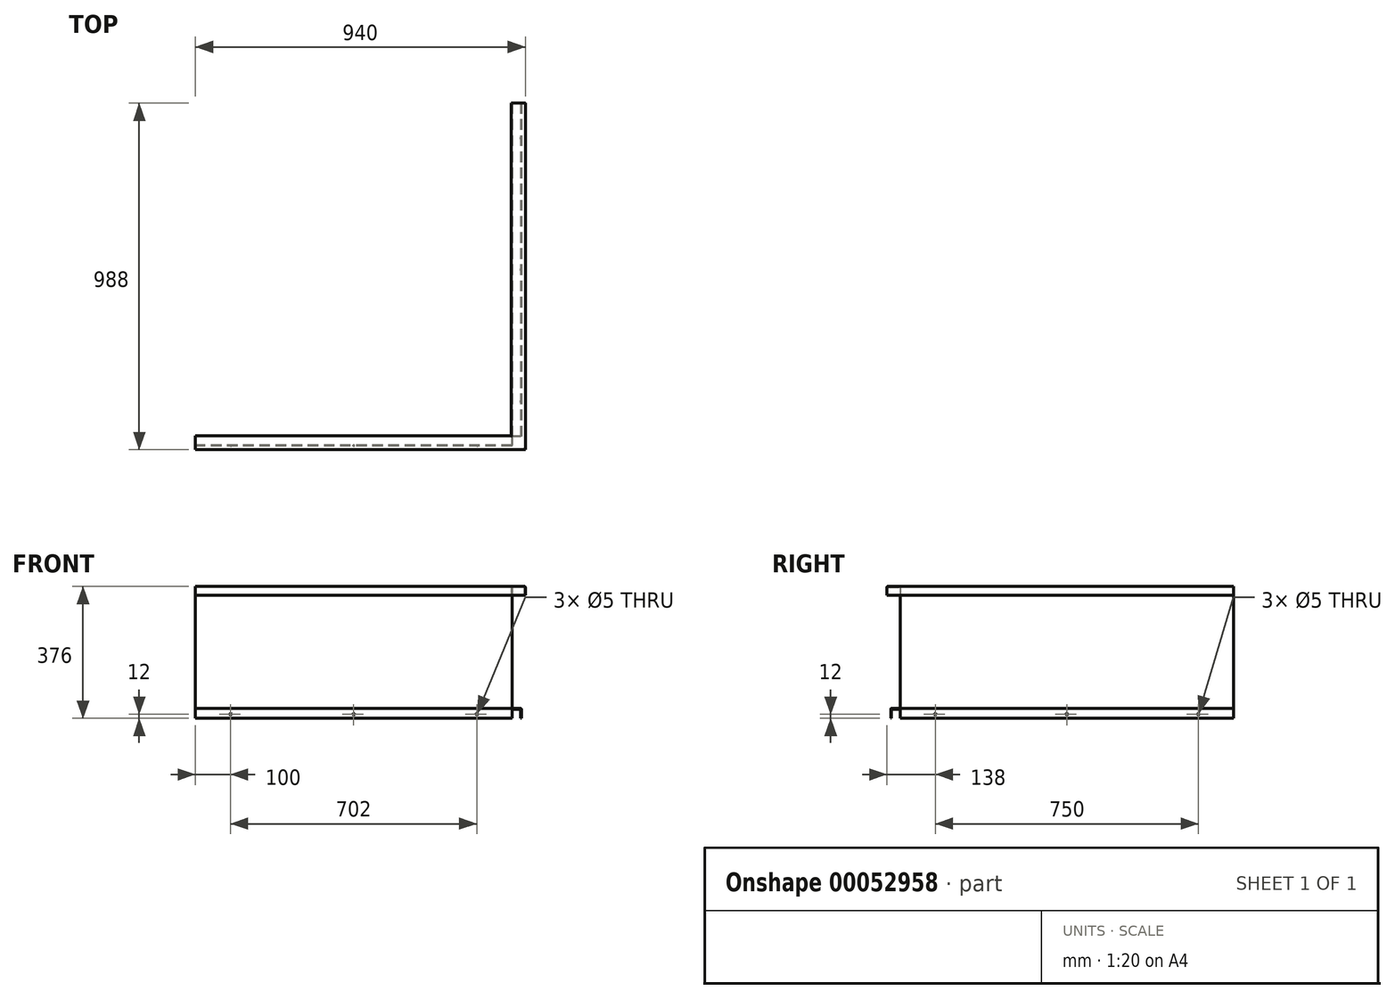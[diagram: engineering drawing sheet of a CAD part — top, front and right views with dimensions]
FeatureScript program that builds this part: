
annotation { "Feature Type Name" : "Feature", "Feature Type Description" : "" }
export const myFeature = defineFeature(function(context is Context, id is Id, definition is map)
    precondition{}
    {
        {
            var Q0;
            Q0=qCreatedBy(makeId("Front.planeOp"),FACE);
            var sketch = newSketch(context, id + "F0", { "sketchPlane" : qUnion([Q0])});
            skLineSegment(sketch, "E0", {"start": v(38, -25) * mm, "end": v(38, -2) * mm});
            skLineSegment(sketch, "E1", {"start": v(38, -2) * mm, "end": v(2, -2) * mm});
            skLineSegment(sketch, "E2", {"start": v(2, -2) * mm, "end": v(2, -348) * mm});
            skLineSegment(sketch, "E3", {"start": v(2, -348) * mm, "end": v(29, -348) * mm});
            skLineSegment(sketch, "E4", {"start": v(29, -348) * mm, "end": v(29, -376) * mm});
            skLineSegment(sketch, "E5.0", {"start": v(27, -350) * mm, "end": v(27, -376) * mm});
            skLineSegment(sketch, "E5.1", {"start": v(40, -25) * mm, "end": v(40, 0) * mm});
            skLineSegment(sketch, "E5.2", {"start": v(40, 0) * mm, "end": v(0, 0) * mm});
            skLineSegment(sketch, "E5.3", {"start": v(0, 0) * mm, "end": v(0, -350) * mm});
            skLineSegment(sketch, "E5.4", {"start": v(0, -350) * mm, "end": v(27, -350) * mm});
            skLineSegment(sketch, "E6", {"start": v(27, -376) * mm, "end": v(29, -376) * mm});
            skLineSegment(sketch, "E7", {"start": v(38, -25) * mm, "end": v(40, -25) * mm});
            skSolve(sketch);
        }
        {
            var Q0;
            Q0=qCreatedBy(makeId("Top.planeOp"),FACE);
            var sketch = newSketch(context, id + "F1", { "sketchPlane" : qUnion([Q0])});
            skLineSegment(sketch, "E8", {"start": v(0, 0) * mm, "end": v(0, -948) * mm});
            skLineSegment(sketch, "E9", {"start": v(0, -948) * mm, "end": v(-900, -948) * mm});
            skSolve(sketch);
        }
        {
            var Q0;
            Q0 = qSketchRegion(id + "F0", true);
            var Q1;
            Q1 = qConstructionFilter(qBodyType(qCreatedBy(id + "F1" ,EDGE), BodyType.WIRE), ConstructionObject.NO);
            sweep(context, id + "F2", {"profiles" : qUnion([Q0]), "path" : qUnion([Q1])});
        }
        {
            var Q0;
            Q0=makeQuery(id+"F2.opSweep","SWEPT_FACE",FACE,{"disambiguationData":[OSD([sQuery(id+"F0.wireOp",EDGE,"E3"),sQuery(id+"F1.wireOp",EDGE,"E8")])]});
            var sketch = newSketch(context, id + "F3", { "sketchPlane" : qUnion([Q0])});
            skLineSegment(sketch, "E10.bottom", {"start": v(2, -950) * mm, "end": v(29, -950) * mm});
            skLineSegment(sketch, "E10.top", {"start": v(2, -977) * mm, "end": v(29, -977) * mm});
            skLineSegment(sketch, "E10.left", {"start": v(2, -950) * mm, "end": v(2, -977) * mm});
            skLineSegment(sketch, "E10.right", {"start": v(29, -950) * mm, "end": v(29, -977) * mm});
            skSolve(sketch);
        }
        {
            var Q0;
            Q0 = qSketchRegion(id + "F3", true);
            extrude(context, id + "F4", {"entities" : qUnion([Q0]), "operationType" : NewBodyOperationType.REMOVE, "oppositeDirection" : true, "depth" : 30 * mm});
        }
        {
            var Q0;
            Q0=makeQuery(id+"F2.opSweep","SWEPT_EDGE",EDGE,{"disambiguationData":[OSD([sQuery(id+"F0.wireOp",EDGE,"E3"),sQuery(id+"F0.wireOp",EDGE,"E4"),sQuery(id+"F1.wireOp",EDGE,"E8")])]});
            var Q1;
            Q1=makeQuery(id+"F2.opSweep","SWEPT_EDGE",EDGE,{"disambiguationData":[OSD([sQuery(id+"F0.wireOp",EDGE,"E2"),sQuery(id+"F0.wireOp",EDGE,"E3"),sQuery(id+"F1.wireOp",EDGE,"E8")])]});
            var Q2;
            Q2=makeQuery(id+"F2.opSweep","SWEPT_EDGE",EDGE,{"disambiguationData":[OSD([sQuery(id+"F0.wireOp",EDGE,"E5.1"),sQuery(id+"F0.wireOp",EDGE,"E5.2"),sQuery(id+"F1.wireOp",EDGE,"E8")])]});
            var Q3;
            Q3=makeQuery(id+"F2.opSweep","SWEPT_EDGE",EDGE,{"disambiguationData":[OSD([sQuery(id+"F0.wireOp",EDGE,"E5.2"),sQuery(id+"F0.wireOp",EDGE,"E5.3"),sQuery(id+"F1.wireOp",EDGE,"E8")])]});
            var Q4;
            Q4=makeQuery(id+"F2.opSweep","SWEPT_EDGE",EDGE,{"disambiguationData":[OSD([sQuery(id+"F0.wireOp",EDGE,"E5.0"),sQuery(id+"F0.wireOp",EDGE,"E5.4"),sQuery(id+"F1.wireOp",EDGE,"E8")])]});
            var Q5;
            Q5=makeQuery(id+"F2.opSweep","SWEPT_EDGE",EDGE,{"disambiguationData":[OSD([sQuery(id+"F0.wireOp",EDGE,"E5.3"),sQuery(id+"F0.wireOp",EDGE,"E5.4"),sQuery(id+"F1.wireOp",EDGE,"E8")])]});
            var Q6;
            Q6=makeQuery(id+"F2.opSweep","SWEPT_EDGE",EDGE,{"disambiguationData":[OSD([sQuery(id+"F0.wireOp",EDGE,"E0"),sQuery(id+"F0.wireOp",EDGE,"E1"),sQuery(id+"F1.wireOp",EDGE,"E8")])]});
            var Q7;
            Q7=makeQuery(id+"F2.opSweep","SWEPT_EDGE",EDGE,{"disambiguationData":[OSD([sQuery(id+"F0.wireOp",EDGE,"E1"),sQuery(id+"F0.wireOp",EDGE,"E2"),sQuery(id+"F1.wireOp",EDGE,"E8")])]});
            var Q8;
            Q8=makeQuery(id+"F2.opSweep","SWEPT_EDGE",EDGE,{"disambiguationData":[OSD([sQuery(id+"F0.wireOp",EDGE,"E5.1"),sQuery(id+"F0.wireOp",EDGE,"E5.2"),sQuery(id+"F1.wireOp",EDGE,"E9")])]});
            var Q9;
            Q9=makeQuery(id+"F2.opSweep","SWEPT_EDGE",EDGE,{"disambiguationData":[OSD([sQuery(id+"F0.wireOp",EDGE,"E5.2"),sQuery(id+"F0.wireOp",EDGE,"E5.3"),sQuery(id+"F1.wireOp",EDGE,"E9")])]});
            var Q10;
            Q10=makeQuery(id+"F2.opSweep","SWEPT_EDGE",EDGE,{"disambiguationData":[OSD([sQuery(id+"F0.wireOp",EDGE,"E5.3"),sQuery(id+"F0.wireOp",EDGE,"E5.4"),sQuery(id+"F1.wireOp",EDGE,"E9")])]});
            var Q11;
            Q11=makeQuery(id+"F2.opSweep","SWEPT_EDGE",EDGE,{"disambiguationData":[OSD([sQuery(id+"F0.wireOp",EDGE,"E5.0"),sQuery(id+"F0.wireOp",EDGE,"E5.4"),sQuery(id+"F1.wireOp",EDGE,"E9")])]});
            var Q12;
            Q12=makeQuery(id+"F2.opSweep","SWEPT_EDGE",EDGE,{"disambiguationData":[OSD([sQuery(id+"F0.wireOp",EDGE,"E3"),sQuery(id+"F0.wireOp",EDGE,"E4"),sQuery(id+"F1.wireOp",EDGE,"E9")])]});
            var Q13;
            Q13=makeQuery(id+"F2.opSweep","SWEPT_EDGE",EDGE,{"disambiguationData":[OSD([sQuery(id+"F0.wireOp",EDGE,"E0"),sQuery(id+"F0.wireOp",EDGE,"E1"),sQuery(id+"F1.wireOp",EDGE,"E9")])]});
            var Q14;
            Q14=makeQuery(id+"F2.opSweep","SWEPT_EDGE",EDGE,{"disambiguationData":[OSD([sQuery(id+"F0.wireOp",EDGE,"E1"),sQuery(id+"F0.wireOp",EDGE,"E2"),sQuery(id+"F1.wireOp",EDGE,"E9")])]});
            fillet(context, id + "F5", {"entities" : qUnion([Q0, Q1, Q2, Q3, Q4, Q5, Q6, Q7, Q8, Q9, Q10, Q11, Q12, Q13, Q14]), "radius" : 2 * mm, "tangentPropagation" : true, "allowEdgeOverflow" : false});
        }
        {
            var Q0;
            Q0=makeQuery(id+"F2.opSweep","SWEPT_FACE",FACE,{"disambiguationData":[OSD([sQuery(id+"F0.wireOp",EDGE,"E5.0"),sQuery(id+"F1.wireOp",EDGE,"E8")])]});
            var sketch = newSketch(context, id + "F6", { "sketchPlane" : qUnion([Q0])});
            skLineSegment(sketch, "E11", {"start": v(950, -364) * mm, "end": v(0, -364) * mm, "construction": true});
            skPoint(sketch, "E12", {"position": v(850, -364) * mm});
            skPoint(sketch, "E13", {"position": v(475, -364) * mm});
            skPoint(sketch, "E14", {"position": v(100, -364) * mm});
            skSolve(sketch);
        }
        {
            var Q0;
            Q0=makeQuery(id+"F2.opSweep","SWEPT_FACE",FACE,{"disambiguationData":[OSD([sQuery(id+"F0.wireOp",EDGE,"E5.0"),sQuery(id+"F1.wireOp",EDGE,"E9")])]});
            var sketch = newSketch(context, id + "F7", { "sketchPlane" : qUnion([Q0])});
            skPoint(sketch, "E15", {"position": v(800, -364) * mm});
            skPoint(sketch, "E16", {"position": v(449, -364) * mm});
            skPoint(sketch, "E17", {"position": v(98, -364) * mm});
            skLineSegment(sketch, "E18", {"start": v(-2, -364) * mm, "end": v(900, -364) * mm, "construction": true});
            skSolve(sketch);
        }
        {
            var Q0;
            Q0=sQuery(id+"F7.wireOp",VERTEX,"E17");
            var Q1;
            Q1=sQuery(id+"F7.wireOp",VERTEX,"E16");
            var Q2;
            Q2=sQuery(id+"F7.wireOp",VERTEX,"E15");
            var Q3;
            Q3=sQuery(id+"F6.wireOp",VERTEX,"E14");
            var Q4;
            Q4=sQuery(id+"F6.wireOp",VERTEX,"E13");
            var Q5;
            Q5=sQuery(id+"F6.wireOp",VERTEX,"E12");
            var Q6;
            Q6=makeQuery(id+"F2.opSweep","SWEPT_BODY",BODY,{"disambiguationData":[OSD([sQuery(id+"F0.wireOp",EDGE,"E0"),sQuery(id+"F0.wireOp",EDGE,"E1"),sQuery(id+"F0.wireOp",EDGE,"E2"),sQuery(id+"F0.wireOp",EDGE,"E3"),sQuery(id+"F0.wireOp",EDGE,"E4"),sQuery(id+"F0.wireOp",EDGE,"E5.0"),sQuery(id+"F0.wireOp",EDGE,"E5.1"),sQuery(id+"F0.wireOp",EDGE,"E5.2"),sQuery(id+"F0.wireOp",EDGE,"E5.3"),sQuery(id+"F0.wireOp",EDGE,"E5.4"),sQuery(id+"F0.wireOp",EDGE,"E6"),sQuery(id+"F0.wireOp",EDGE,"E7"),sQuery(id+"F1.wireOp",EDGE,"E9")])]});
            hole(context, id + "F8", {"style" : HoleStyle.SIMPLE, "holeDiameter" : 5 * mm, "endStyle" : HoleEndStyle.THROUGH, "locations" : qUnion([Q0, Q1, Q2, Q3, Q4, Q5]), "scope" : qUnion([Q6])});
        }
    });
